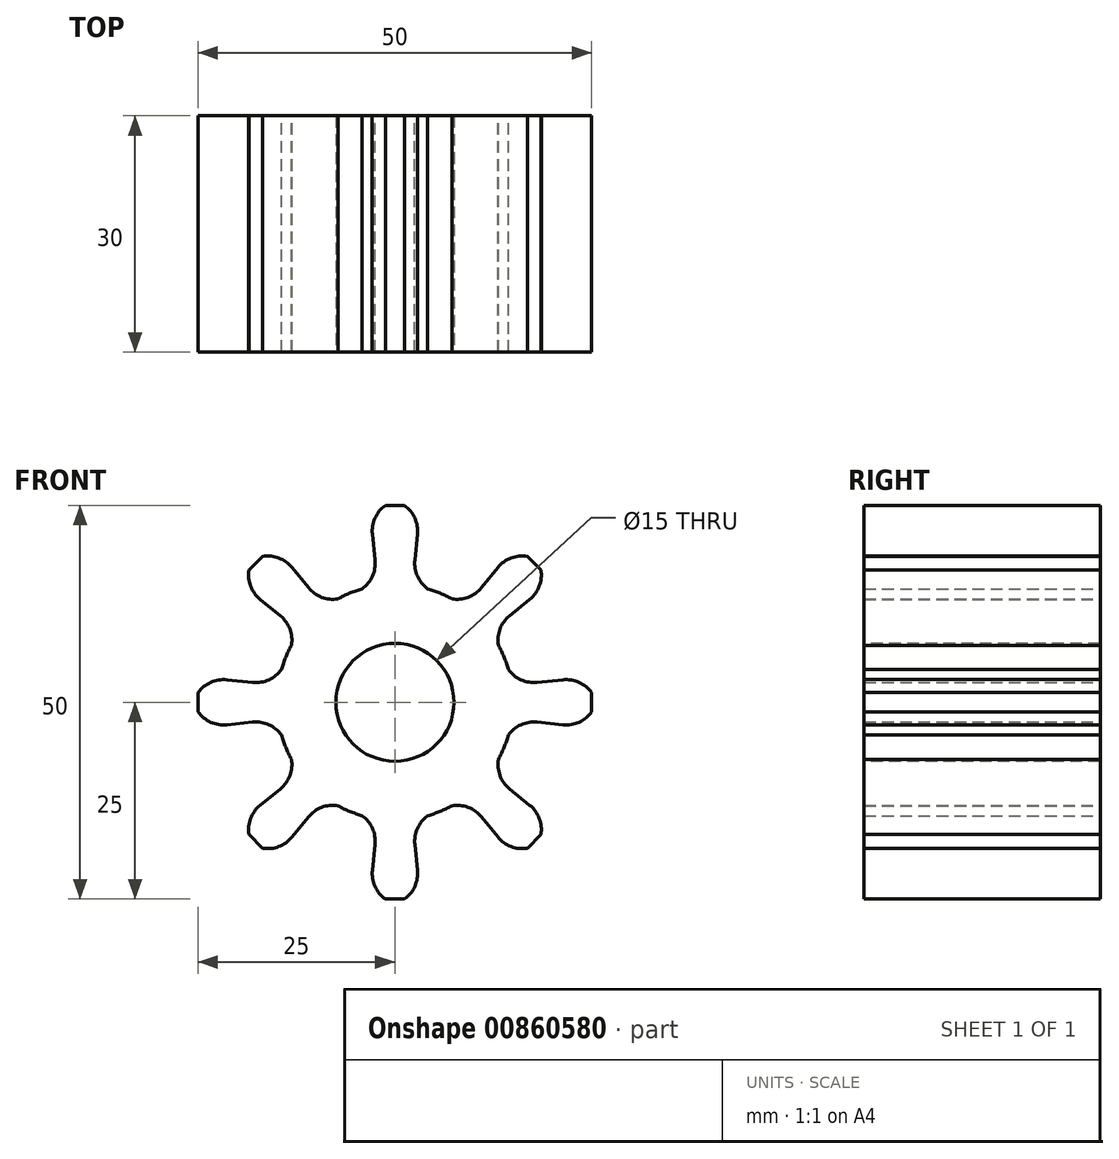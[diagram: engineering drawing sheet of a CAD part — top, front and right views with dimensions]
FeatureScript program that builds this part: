
annotation { "Feature Type Name" : "Feature", "Feature Type Description" : "" }
export const myFeature = defineFeature(function(context is Context, id is Id, definition is map)
    precondition{}
    {
        {
            var Q0;
            Q0=qCreatedBy(makeId("Front.planeOp"),FACE);
            var sketch = newSketch(context, id + "F0", { "sketchPlane" : qUnion([Q0])});
            skArc(sketch, "E0", {"start": v(-13.14, 7.24) * mm, "mid": v(-13.86, 5.74) * mm, "end": v(-14.4, 4.17) * mm});
            skArc(sketch, "E1", {"start": v(-4.17, 14.4) * mm, "mid": v(-2.86, 16.01) * mm, "end": v(-2.53, 18.06) * mm});
            skLineSegment(sketch, "E2", {"start": v(-2.53, 18.06) * mm, "end": v(-2.86, 21.35) * mm});
            skLineSegment(sketch, "E3", {"start": v(-1.22, 25) * mm, "end": v(1.22, 25) * mm});
            skArc(sketch, "E4", {"start": v(-1.22, 25) * mm, "mid": v(-2.53, 23.4) * mm, "end": v(-2.86, 21.35) * mm});
            skArc(sketch, "E5.MirrorCS", {"start": v(1.22, 25) * mm, "mid": v(2.53, 23.4) * mm, "end": v(2.86, 21.35) * mm});
            skLineSegment(sketch, "E6.MirrorCS", {"start": v(2.53, 18.06) * mm, "end": v(2.86, 21.35) * mm});
            skArc(sketch, "E7.MirrorCS", {"start": v(4.17, 14.4) * mm, "mid": v(2.86, 16.01) * mm, "end": v(2.53, 18.06) * mm});
            skLineSegment(sketch, "E8.1.0", {"start": v(-18.54, 16.81) * mm, "end": v(-16.81, 18.54) * mm});
            skArc(sketch, "E8.1.1", {"start": v(-18.54, 16.81) * mm, "mid": v(-18.33, 14.75) * mm, "end": v(-17.12, 13.07) * mm});
            skLineSegment(sketch, "E8.1.2", {"start": v(-14.56, 10.98) * mm, "end": v(-17.12, 13.07) * mm});
            skArc(sketch, "E8.1.3", {"start": v(-13.14, 7.24) * mm, "mid": v(-13.34, 9.3) * mm, "end": v(-14.56, 10.98) * mm});
            skArc(sketch, "E8.1.4", {"start": v(-7.24, 13.14) * mm, "mid": v(-9.3, 13.34) * mm, "end": v(-10.98, 14.56) * mm});
            skLineSegment(sketch, "E8.1.5", {"start": v(-10.98, 14.56) * mm, "end": v(-13.07, 17.12) * mm});
            skArc(sketch, "E8.1.6", {"start": v(-16.81, 18.54) * mm, "mid": v(-14.75, 18.33) * mm, "end": v(-13.07, 17.12) * mm});
            skLineSegment(sketch, "E8.2.0", {"start": v(-25, -1.22) * mm, "end": v(-25, 1.22) * mm});
            skArc(sketch, "E8.2.1", {"start": v(-25, -1.22) * mm, "mid": v(-23.4, -2.53) * mm, "end": v(-21.35, -2.86) * mm});
            skLineSegment(sketch, "E8.2.2", {"start": v(-18.06, -2.53) * mm, "end": v(-21.35, -2.86) * mm});
            skArc(sketch, "E8.2.3", {"start": v(-14.4, -4.17) * mm, "mid": v(-16.01, -2.86) * mm, "end": v(-18.06, -2.53) * mm});
            skArc(sketch, "E8.2.4", {"start": v(-14.4, 4.17) * mm, "mid": v(-16.01, 2.86) * mm, "end": v(-18.06, 2.53) * mm});
            skLineSegment(sketch, "E8.2.5", {"start": v(-18.06, 2.53) * mm, "end": v(-21.35, 2.86) * mm});
            skArc(sketch, "E8.2.6", {"start": v(-25, 1.22) * mm, "mid": v(-23.4, 2.53) * mm, "end": v(-21.35, 2.86) * mm});
            skLineSegment(sketch, "E8.3.0", {"start": v(-16.81, -18.54) * mm, "end": v(-18.54, -16.81) * mm});
            skArc(sketch, "E8.3.1", {"start": v(-16.81, -18.54) * mm, "mid": v(-14.75, -18.33) * mm, "end": v(-13.07, -17.12) * mm});
            skLineSegment(sketch, "E8.3.2", {"start": v(-10.98, -14.56) * mm, "end": v(-13.07, -17.12) * mm});
            skArc(sketch, "E8.3.3", {"start": v(-7.24, -13.14) * mm, "mid": v(-9.3, -13.34) * mm, "end": v(-10.98, -14.56) * mm});
            skArc(sketch, "E8.3.4", {"start": v(-13.14, -7.24) * mm, "mid": v(-13.34, -9.3) * mm, "end": v(-14.56, -10.98) * mm});
            skLineSegment(sketch, "E8.3.5", {"start": v(-14.56, -10.98) * mm, "end": v(-17.12, -13.07) * mm});
            skArc(sketch, "E8.3.6", {"start": v(-18.54, -16.81) * mm, "mid": v(-18.33, -14.75) * mm, "end": v(-17.12, -13.07) * mm});
            skLineSegment(sketch, "E8.4.0", {"start": v(1.22, -25) * mm, "end": v(-1.22, -25) * mm});
            skArc(sketch, "E8.4.1", {"start": v(1.22, -25) * mm, "mid": v(2.53, -23.4) * mm, "end": v(2.86, -21.35) * mm});
            skLineSegment(sketch, "E8.4.2", {"start": v(2.53, -18.06) * mm, "end": v(2.86, -21.35) * mm});
            skArc(sketch, "E8.4.3", {"start": v(4.17, -14.4) * mm, "mid": v(2.86, -16.01) * mm, "end": v(2.53, -18.06) * mm});
            skArc(sketch, "E8.4.4", {"start": v(-4.17, -14.4) * mm, "mid": v(-2.86, -16.01) * mm, "end": v(-2.53, -18.06) * mm});
            skLineSegment(sketch, "E8.4.5", {"start": v(-2.53, -18.06) * mm, "end": v(-2.86, -21.35) * mm});
            skArc(sketch, "E8.4.6", {"start": v(-1.22, -25) * mm, "mid": v(-2.53, -23.4) * mm, "end": v(-2.86, -21.35) * mm});
            skLineSegment(sketch, "E8.5.0", {"start": v(18.54, -16.81) * mm, "end": v(16.81, -18.54) * mm});
            skArc(sketch, "E8.5.1", {"start": v(18.54, -16.81) * mm, "mid": v(18.33, -14.75) * mm, "end": v(17.12, -13.07) * mm});
            skLineSegment(sketch, "E8.5.2", {"start": v(14.56, -10.98) * mm, "end": v(17.12, -13.07) * mm});
            skArc(sketch, "E8.5.3", {"start": v(13.14, -7.24) * mm, "mid": v(13.34, -9.3) * mm, "end": v(14.56, -10.98) * mm});
            skArc(sketch, "E8.5.4", {"start": v(7.24, -13.14) * mm, "mid": v(9.3, -13.34) * mm, "end": v(10.98, -14.56) * mm});
            skLineSegment(sketch, "E8.5.5", {"start": v(10.98, -14.56) * mm, "end": v(13.07, -17.12) * mm});
            skArc(sketch, "E8.5.6", {"start": v(16.81, -18.54) * mm, "mid": v(14.75, -18.33) * mm, "end": v(13.07, -17.12) * mm});
            skLineSegment(sketch, "E8.6.0", {"start": v(25, 1.22) * mm, "end": v(25, -1.22) * mm});
            skArc(sketch, "E8.6.1", {"start": v(25, 1.22) * mm, "mid": v(23.4, 2.53) * mm, "end": v(21.35, 2.86) * mm});
            skLineSegment(sketch, "E8.6.2", {"start": v(18.06, 2.53) * mm, "end": v(21.35, 2.86) * mm});
            skArc(sketch, "E8.6.3", {"start": v(14.4, 4.17) * mm, "mid": v(16.01, 2.86) * mm, "end": v(18.06, 2.53) * mm});
            skArc(sketch, "E8.6.4", {"start": v(14.4, -4.17) * mm, "mid": v(16.01, -2.86) * mm, "end": v(18.06, -2.53) * mm});
            skLineSegment(sketch, "E8.6.5", {"start": v(18.06, -2.53) * mm, "end": v(21.35, -2.86) * mm});
            skArc(sketch, "E8.6.6", {"start": v(25, -1.22) * mm, "mid": v(23.4, -2.53) * mm, "end": v(21.35, -2.86) * mm});
            skLineSegment(sketch, "E8.7.0", {"start": v(16.81, 18.54) * mm, "end": v(18.54, 16.81) * mm});
            skArc(sketch, "E8.7.1", {"start": v(16.81, 18.54) * mm, "mid": v(14.75, 18.33) * mm, "end": v(13.07, 17.12) * mm});
            skLineSegment(sketch, "E8.7.2", {"start": v(10.98, 14.56) * mm, "end": v(13.07, 17.12) * mm});
            skArc(sketch, "E8.7.3", {"start": v(7.24, 13.14) * mm, "mid": v(9.3, 13.34) * mm, "end": v(10.98, 14.56) * mm});
            skArc(sketch, "E8.7.4", {"start": v(13.14, 7.24) * mm, "mid": v(13.34, 9.3) * mm, "end": v(14.56, 10.98) * mm});
            skLineSegment(sketch, "E8.7.5", {"start": v(14.56, 10.98) * mm, "end": v(17.12, 13.07) * mm});
            skArc(sketch, "E8.7.6", {"start": v(18.54, 16.81) * mm, "mid": v(18.33, 14.75) * mm, "end": v(17.12, 13.07) * mm});
            skArc(sketch, "E9.trimOffspring", {"start": v(-4.17, 14.4) * mm, "mid": v(-5.74, 13.86) * mm, "end": v(-7.24, 13.14) * mm});
            skArc(sketch, "E10.trimOffspring", {"start": v(7.24, 13.14) * mm, "mid": v(5.74, 13.86) * mm, "end": v(4.17, 14.4) * mm});
            skArc(sketch, "E11.trimOffspring", {"start": v(14.4, 4.17) * mm, "mid": v(13.86, 5.74) * mm, "end": v(13.14, 7.24) * mm});
            skArc(sketch, "E12.trimOffspring", {"start": v(13.14, -7.24) * mm, "mid": v(13.86, -5.74) * mm, "end": v(14.4, -4.17) * mm});
            skArc(sketch, "E13.trimOffspring", {"start": v(4.17, -14.4) * mm, "mid": v(5.74, -13.86) * mm, "end": v(7.24, -13.14) * mm});
            skArc(sketch, "E14.trimOffspring", {"start": v(-7.24, -13.14) * mm, "mid": v(-5.74, -13.86) * mm, "end": v(-4.17, -14.4) * mm});
            skArc(sketch, "E15.trimOffspring", {"start": v(-14.4, -4.17) * mm, "mid": v(-13.86, -5.74) * mm, "end": v(-13.14, -7.24) * mm});
            skSolve(sketch);
        }
        {
            var Q0;
            Q0 = qSketchRegion(id + "F0", true);
            extrude(context, id + "F1", {"entities" : qUnion([Q0]), "depth" : 30 * mm, "offsetDistance" : 25 * mm});
        }
        {
            var Q0;
            Q0=makeQuery(id+"F1.opExtrude","CAP_FACE",FACE,{"disambiguationData":[OSD([sQuery(id+"F0.wireOp",EDGE,"E0"),sQuery(id+"F0.wireOp",EDGE,"E1"),sQuery(id+"F0.wireOp",EDGE,"E2"),sQuery(id+"F0.wireOp",EDGE,"E3"),sQuery(id+"F0.wireOp",EDGE,"E4"),sQuery(id+"F0.wireOp",EDGE,"E5.MirrorCS"),sQuery(id+"F0.wireOp",EDGE,"E6.MirrorCS"),sQuery(id+"F0.wireOp",EDGE,"E7.MirrorCS"),sQuery(id+"F0.wireOp",EDGE,"E8.1.0"),sQuery(id+"F0.wireOp",EDGE,"E8.1.1"),sQuery(id+"F0.wireOp",EDGE,"E8.1.2"),sQuery(id+"F0.wireOp",EDGE,"E8.1.3"),sQuery(id+"F0.wireOp",EDGE,"E8.1.4"),sQuery(id+"F0.wireOp",EDGE,"E8.1.5"),sQuery(id+"F0.wireOp",EDGE,"E8.1.6"),sQuery(id+"F0.wireOp",EDGE,"E8.2.0"),sQuery(id+"F0.wireOp",EDGE,"E8.2.1"),sQuery(id+"F0.wireOp",EDGE,"E8.2.2"),sQuery(id+"F0.wireOp",EDGE,"E8.2.3"),sQuery(id+"F0.wireOp",EDGE,"E8.2.4"),sQuery(id+"F0.wireOp",EDGE,"E8.2.5"),sQuery(id+"F0.wireOp",EDGE,"E8.2.6"),sQuery(id+"F0.wireOp",EDGE,"E8.3.0"),sQuery(id+"F0.wireOp",EDGE,"E8.3.1"),sQuery(id+"F0.wireOp",EDGE,"E8.3.2"),sQuery(id+"F0.wireOp",EDGE,"E8.3.3"),sQuery(id+"F0.wireOp",EDGE,"E8.3.4"),sQuery(id+"F0.wireOp",EDGE,"E8.3.5"),sQuery(id+"F0.wireOp",EDGE,"E8.3.6"),sQuery(id+"F0.wireOp",EDGE,"E8.4.0"),sQuery(id+"F0.wireOp",EDGE,"E8.4.1"),sQuery(id+"F0.wireOp",EDGE,"E8.4.2"),sQuery(id+"F0.wireOp",EDGE,"E8.4.3"),sQuery(id+"F0.wireOp",EDGE,"E8.4.4"),sQuery(id+"F0.wireOp",EDGE,"E8.4.5"),sQuery(id+"F0.wireOp",EDGE,"E8.4.6"),sQuery(id+"F0.wireOp",EDGE,"E8.5.0"),sQuery(id+"F0.wireOp",EDGE,"E8.5.1"),sQuery(id+"F0.wireOp",EDGE,"E8.5.2"),sQuery(id+"F0.wireOp",EDGE,"E8.5.3"),sQuery(id+"F0.wireOp",EDGE,"E8.5.4"),sQuery(id+"F0.wireOp",EDGE,"E8.5.5"),sQuery(id+"F0.wireOp",EDGE,"E8.5.6"),sQuery(id+"F0.wireOp",EDGE,"E8.6.0"),sQuery(id+"F0.wireOp",EDGE,"E8.6.1"),sQuery(id+"F0.wireOp",EDGE,"E8.6.2"),sQuery(id+"F0.wireOp",EDGE,"E8.6.3"),sQuery(id+"F0.wireOp",EDGE,"E8.6.4"),sQuery(id+"F0.wireOp",EDGE,"E8.6.5"),sQuery(id+"F0.wireOp",EDGE,"E8.6.6"),sQuery(id+"F0.wireOp",EDGE,"E8.7.0"),sQuery(id+"F0.wireOp",EDGE,"E8.7.1"),sQuery(id+"F0.wireOp",EDGE,"E8.7.2"),sQuery(id+"F0.wireOp",EDGE,"E8.7.3"),sQuery(id+"F0.wireOp",EDGE,"E8.7.4"),sQuery(id+"F0.wireOp",EDGE,"E8.7.5"),sQuery(id+"F0.wireOp",EDGE,"E8.7.6"),sQuery(id+"F0.wireOp",EDGE,"E9.trimOffspring"),sQuery(id+"F0.wireOp",EDGE,"E10.trimOffspring"),sQuery(id+"F0.wireOp",EDGE,"E11.trimOffspring"),sQuery(id+"F0.wireOp",EDGE,"E12.trimOffspring"),sQuery(id+"F0.wireOp",EDGE,"E13.trimOffspring"),sQuery(id+"F0.wireOp",EDGE,"E14.trimOffspring"),sQuery(id+"F0.wireOp",EDGE,"E15.trimOffspring")])],"isStart":false});
            var sketch = newSketch(context, id + "F2", { "sketchPlane" : qUnion([Q0])});
            skCircle(sketch, "E16", {"center": v(0, 0) * mm, "radius": 7.5 * mm});
            skSolve(sketch);
        }
        {
            var Q0;
            Q0 = qSketchRegion(id + "F2", true);
            extrude(context, id + "F3", {"entities" : qUnion([Q0]), "operationType" : NewBodyOperationType.REMOVE, "endBound" : BoundingType.THROUGH_ALL, "oppositeDirection" : true, "depth" : 25 * mm, "offsetDistance" : 25 * mm});
        }
    });
